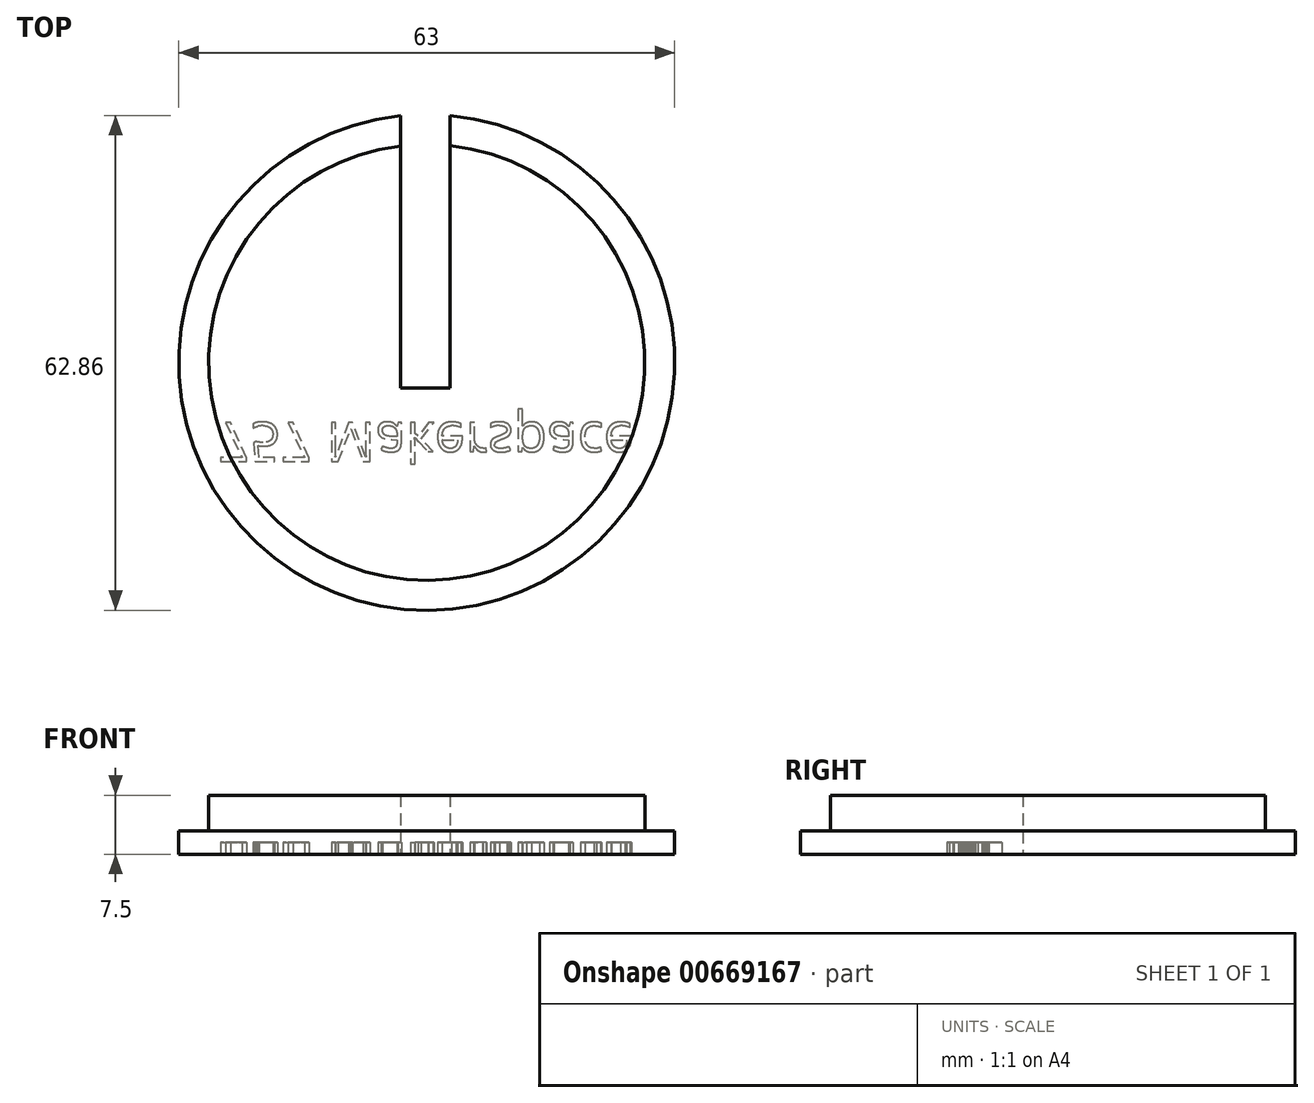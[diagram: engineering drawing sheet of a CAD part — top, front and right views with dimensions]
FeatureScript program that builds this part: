
annotation { "Feature Type Name" : "Feature", "Feature Type Description" : "" }
export const myFeature = defineFeature(function(context is Context, id is Id, definition is map)
    precondition{}
    {
        {
            var Q0;
            Q0=qCreatedBy(makeId("Top.planeOp"),FACE);
            var sketch = newSketch(context, id + "F0", { "sketchPlane" : qUnion([Q0])});
            skCircle(sketch, "E0", {"center": v(0, 0) * mm, "radius": 31.5 * mm});
            skSolve(sketch);
        }
        {
            var Q0;
            Q0=makeQuery(id+"F0.imprint","IMPRINT",FACE,{"disambiguationData":[TD([[makeQuery(id+"F0.imprint","IMPRINT",EDGE,{"derivedFrom":sQuery(id+"F0.wireOp",EDGE,"E0")}),1.0]])]});
            extrude(context, id + "F1", {"entities" : qUnion([Q0]), "depth" : 3 * mm, "offsetDistance" : 25 * mm});
        }
        {
            var Q0;
            Q0=makeQuery(id+"F1.opExtrude","CAP_FACE",FACE,{"disambiguationData":[OSD([sQuery(id+"F0.wireOp",EDGE,"E0")])],"isStart":false});
            var sketch = newSketch(context, id + "F2", { "sketchPlane" : qUnion([Q0])});
            skCircle(sketch, "E1.0", {"center": v(0, 0) * mm, "radius": 27.7 * mm});
            skSolve(sketch);
        }
        {
            var Q0;
            Q0 = qSketchRegion(id + "F2", true);
            extrude(context, id + "F3", {"entities" : qUnion([Q0]), "operationType" : NewBodyOperationType.ADD, "depth" : 4.5 * mm, "offsetDistance" : 25 * mm});
        }
        {
            var Q0;
            Q0=makeQuery(id+"F1.opExtrude","CAP_FACE",FACE,{"disambiguationData":[OSD([sQuery(id+"F0.wireOp",EDGE,"E0")])],"isStart":true});
            var sketch = newSketch(context, id + "F4", { "sketchPlane" : qUnion([Q0])});
            skLineSegment(sketch, "E2.bottom", {"start": v(-3.34, 3.24) * mm, "end": v(2.94, 3.24) * mm});
            skLineSegment(sketch, "E2.top", {"start": v(-3.34, -33.04) * mm, "end": v(2.94, -33.04) * mm});
            skLineSegment(sketch, "E2.left", {"start": v(-3.34, 3.24) * mm, "end": v(-3.34, -33.04) * mm});
            skLineSegment(sketch, "E2.right", {"start": v(2.94, 3.24) * mm, "end": v(2.94, -33.04) * mm});
            skSolve(sketch);
        }
        {
            var Q0;
            Q0 = qSketchRegion(id + "F4", true);
            extrude(context, id + "F5", {"entities" : qUnion([Q0]), "operationType" : NewBodyOperationType.REMOVE, "oppositeDirection" : true, "depth" : 25 * mm, "offsetDistance" : 25 * mm});
        }
        {
            var Q0;
            Q0=makeQuery(id+"F1.opExtrude","CAP_FACE",FACE,{"disambiguationData":[OSD([sQuery(id+"F0.wireOp",EDGE,"E0")])],"isStart":true});
            var sketch = newSketch(context, id + "F6", { "sketchPlane" : qUnion([Q0])});
            skText(sketch, "E3", { "text": "757 Makerspace", "fontName": "OpenSans-Regular.ttf"});
            const initialGuessF6  = {"E3": [-0.0265, 0.00762, 1, 0, 0.005]};
            skSetInitialGuess(sketch, initialGuessF6);
            skSolve(sketch);
        }
        {
            var Q0;
            Q0 = qSketchRegion(id + "F6", true);
            extrude(context, id + "F7", {"entities" : qUnion([Q0]), "operationType" : NewBodyOperationType.REMOVE, "oppositeDirection" : true, "depth" : 1.5 * mm, "offsetDistance" : 25 * mm});
        }
    });
